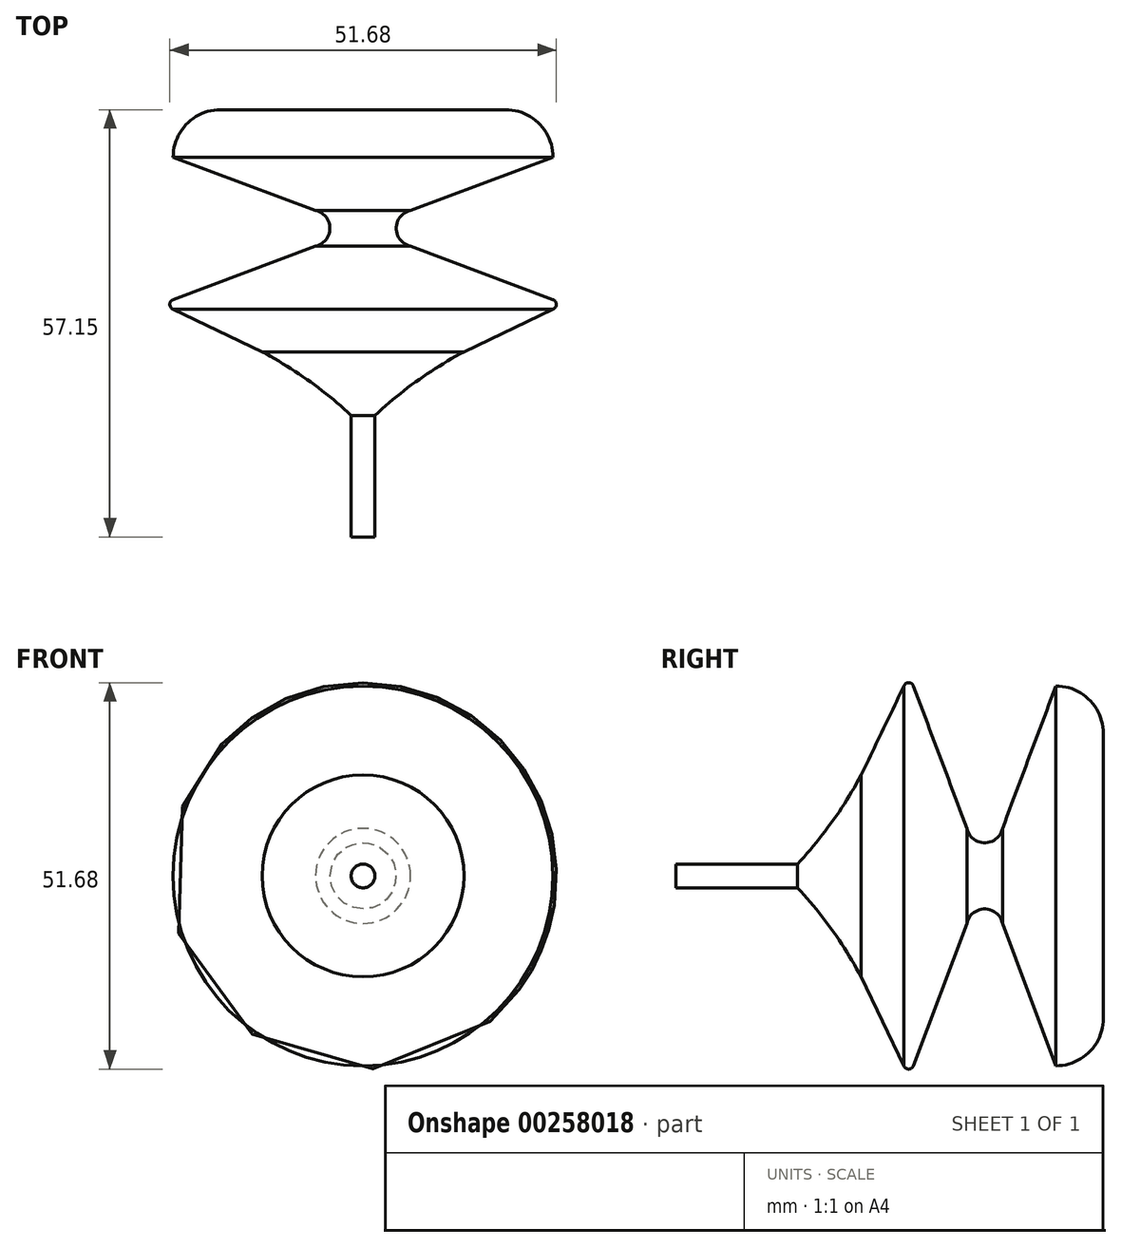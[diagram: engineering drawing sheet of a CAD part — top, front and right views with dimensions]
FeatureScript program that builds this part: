
annotation { "Feature Type Name" : "Feature", "Feature Type Description" : "" }
export const myFeature = defineFeature(function(context is Context, id is Id, definition is map)
    precondition{}
    {
        {
            var Q0;
            Q0=qCreatedBy(makeId("Top.planeOp"),FACE);
            var sketch = newSketch(context, id + "F0", { "sketchPlane" : qUnion([Q0])});
            skLineSegment(sketch, "E0.bottom", {"start": v(0, 0) * mm, "end": v(1.59, 0) * mm});
            skLineSegment(sketch, "E0.left", {"start": v(0, 0) * mm, "end": v(0, 19.05) * mm});
            skLineSegment(sketch, "E0.right", {"start": v(1.59, 0) * mm, "end": v(1.59, 16.26) * mm});
            skLineSegment(sketch, "E1", {"start": v(0, 19.05) * mm, "end": v(0, 31.75) * mm});
            skLineSegment(sketch, "E2", {"start": v(0, 31.75) * mm, "end": v(0, 50.8) * mm});
            skLineSegment(sketch, "E3", {"start": v(0, 50.8) * mm, "end": v(0, -33.32) * mm});
            skLineSegment(sketch, "E4", {"start": v(0, 37.47) * mm, "end": v(0, 50.8) * mm});
            skLineSegment(sketch, "E5.bottom", {"start": v(0, 50.8) * mm, "end": v(0, 50.8) * mm});
            skLineSegment(sketch, "E5.top", {"start": v(0, 31.75) * mm, "end": v(0, 31.75) * mm});
            skLineSegment(sketch, "E5.left", {"start": v(0, 50.8) * mm, "end": v(0, 31.75) * mm});
            skLineSegment(sketch, "E5.right", {"start": v(0, 50.8) * mm, "end": v(0, 31.75) * mm});
            skLineSegment(sketch, "E6", {"start": v(25.4, 50.8) * mm, "end": v(25.4, 50.8) * mm});
            skLineSegment(sketch, "E7", {"start": v(19.05, 57.15) * mm, "end": v(0, 57.15) * mm});
            skLineSegment(sketch, "E8", {"start": v(0, 57.15) * mm, "end": v(0, 50.8) * mm});
            skPoint(sketch, "E9.visualSharp", {"position": v(25.4, 57.15) * mm});
            skArc(sketch, "E9.filletArc", {"start": v(25.4, 50.8) * mm, "mid": v(23.54, 55.3) * mm, "end": v(19.05, 57.15) * mm});
            skLineSegment(sketch, "E10", {"start": v(25.4, 50.8) * mm, "end": v(5.67, 43.4) * mm});
            skLineSegment(sketch, "E11", {"start": v(5.67, 39.15) * mm, "end": v(25.4, 31.75) * mm});
            skArc(sketch, "E12", {"start": v(6.35, 43.66) * mm, "mid": v(4.42, 41.28) * mm, "end": v(6.35, 38.9) * mm});
            skPoint(sketch, "E13.orphan", {"position": v(0, 41.27) * mm});
            skLineSegment(sketch, "E14", {"start": v(25.4, 30.48) * mm, "end": v(13.5, 24.77) * mm});
            skArc(sketch, "E15", {"start": v(25.4, 31.75) * mm, "mid": v(25.84, 31.12) * mm, "end": v(25.4, 30.48) * mm});
            skArc(sketch, "E16", {"start": v(13.5, 24.76) * mm, "mid": v(7.26, 20.9) * mm, "end": v(1.59, 16.26) * mm});
            skPoint(sketch, "E17.orphan", {"position": v(1.59, 19.05) * mm});
            skSolve(sketch);
        }
        {
            var Q0;
            {var subQ1=sQuery(id+"F0.wireOp",EDGE,"E0.bottom");Q0=makeQuery(id+"F0.imprint","IMPRINT",FACE,{"disambiguationData":[TD([[makeQuery(id+"F0.imprint","IMPRINT",EDGE,{"derivedFrom":subQ1}),1.0]])]});}
            var Q1;
            Q1=sQuery(id+"F0.wireOp",EDGE,"E3");
            revolve(context, id + "F1", {"entities" : qUnion([Q0]), "axis" : qUnion([Q1]), "revolveType" : RevolveType.FULL});
        }
    });
